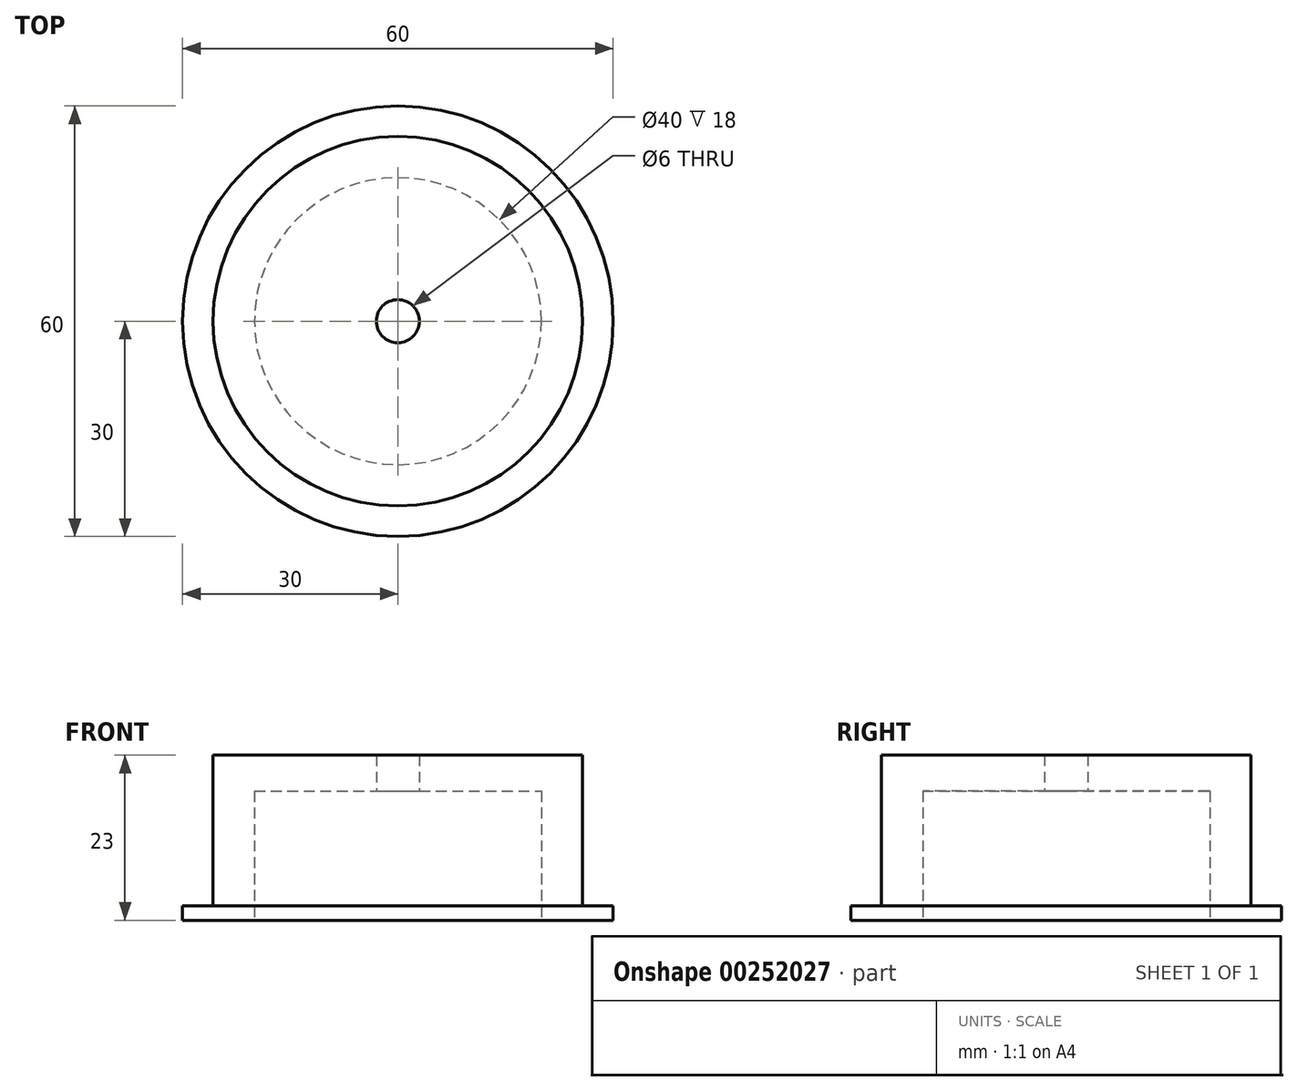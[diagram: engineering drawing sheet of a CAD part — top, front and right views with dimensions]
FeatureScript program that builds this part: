
annotation { "Feature Type Name" : "Feature", "Feature Type Description" : "" }
export const myFeature = defineFeature(function(context is Context, id is Id, definition is map)
    precondition{}
    {
        {
            var Q0;
            Q0=qCreatedBy(makeId("Top.planeOp"),FACE);
            var sketch = newSketch(context, id + "F0", { "sketchPlane" : qUnion([Q0])});
            skCircle(sketch, "E0", {"center": v(0, 0) * mm, "radius": 30 * mm});
            skSolve(sketch);
        }
        {
            var Q0;
            Q0 = qSketchRegion(id + "F0", true);
            extrude(context, id + "F1", {"entities" : qUnion([Q0]), "depth" : 2 * mm});
        }
        {
            var Q0;
            Q0=makeQuery(id+"F1.opExtrude","CAP_FACE",FACE,{"disambiguationData":[OSD([sQuery(id+"F0.wireOp",EDGE,"E0")])],"isStart":false});
            var sketch = newSketch(context, id + "F2", { "sketchPlane" : qUnion([Q0])});
            skCircle(sketch, "E1", {"center": v(0, 0) * mm, "radius": 25.75 * mm});
            skSolve(sketch);
        }
        {
            var Q0;
            Q0 = qSketchRegion(id + "F2", true);
            extrude(context, id + "F3", {"entities" : qUnion([Q0]), "operationType" : NewBodyOperationType.ADD, "depth" : 21 * mm});
        }
        {
            var Q0;
            Q0=makeQuery(id+"F1.opExtrude","CAP_FACE",FACE,{"disambiguationData":[OSD([sQuery(id+"F0.wireOp",EDGE,"E0")])],"isStart":true});
            var sketch = newSketch(context, id + "F4", { "sketchPlane" : qUnion([Q0])});
            skCircle(sketch, "E2", {"center": v(0, 0) * mm, "radius": 20 * mm});
            skSolve(sketch);
        }
        {
            var Q0;
            Q0 = qSketchRegion(id + "F4", true);
            extrude(context, id + "F5", {"entities" : qUnion([Q0]), "operationType" : NewBodyOperationType.REMOVE, "oppositeDirection" : true, "depth" : 18 * mm});
        }
        {
            var Q0;
            Q0=makeQuery(id+"F5.boolean.opBoolean","COPY",FACE,{"derivedFrom":makeQuery(id+"F5.opExtrude","CAP_FACE",FACE,{"disambiguationData":[OSD([sQuery(id+"F4.wireOp",EDGE,"E2")])],"isStart":false})});
            var sketch = newSketch(context, id + "F6", { "sketchPlane" : qUnion([Q0])});
            skCircle(sketch, "E3", {"center": v(0, 0) * mm, "radius": 3 * mm});
            skSolve(sketch);
        }
        {
            var Q0;
            Q0 = qSketchRegion(id + "F6", true);
            extrude(context, id + "F7", {"entities" : qUnion([Q0]), "operationType" : NewBodyOperationType.REMOVE, "endBound" : BoundingType.THROUGH_ALL, "oppositeDirection" : true, "depth" : 25 * mm});
        }
    });
